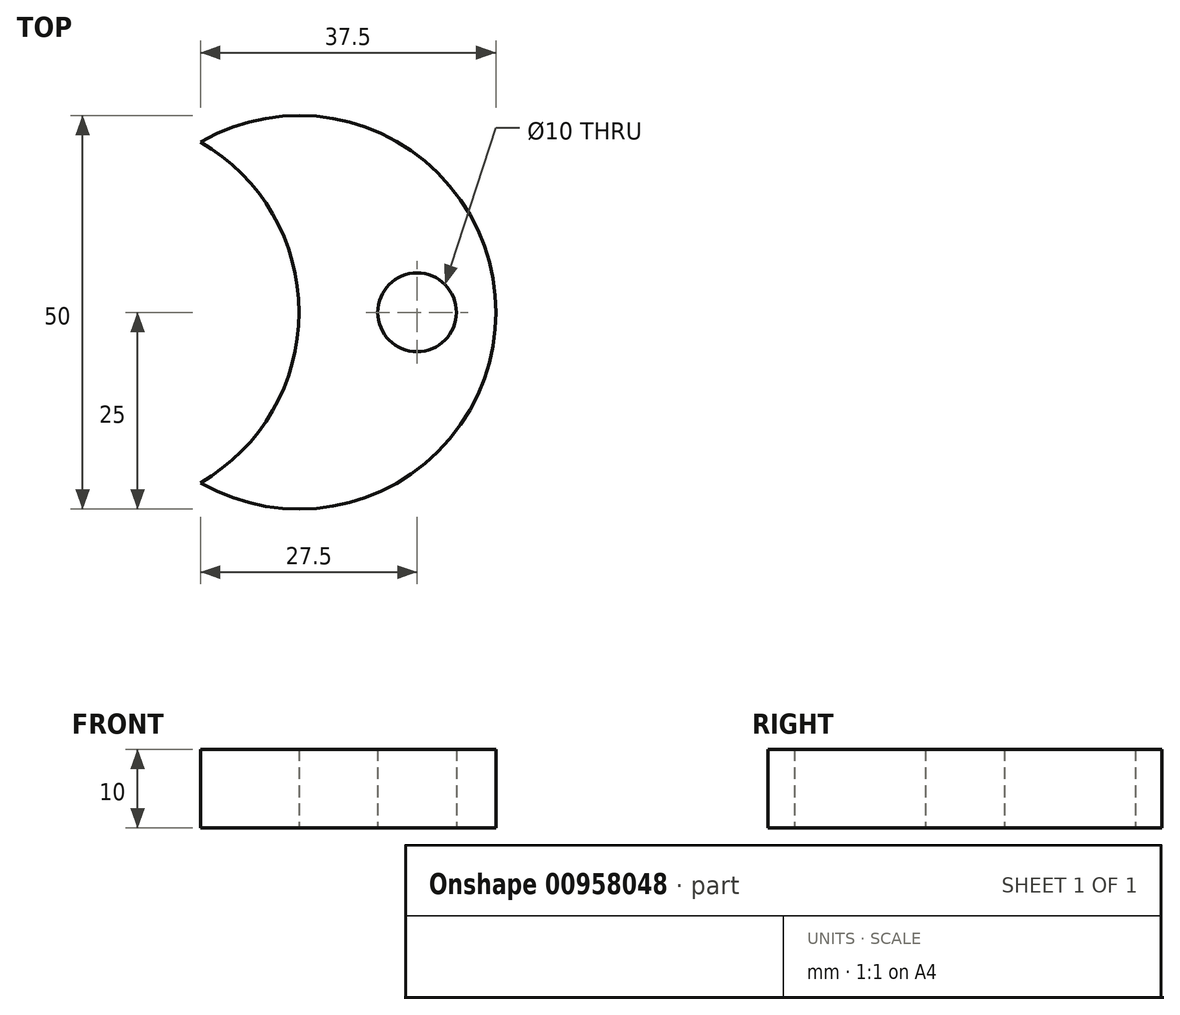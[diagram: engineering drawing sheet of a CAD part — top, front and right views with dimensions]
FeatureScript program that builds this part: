
annotation { "Feature Type Name" : "Feature", "Feature Type Description" : "" }
export const myFeature = defineFeature(function(context is Context, id is Id, definition is map)
    precondition{}
    {
        {
            var Q0;
            Q0=qCreatedBy(makeId("Top.planeOp"),FACE);
            var sketch = newSketch(context, id + "F0", { "sketchPlane" : qUnion([Q0])});
            skCircle(sketch, "E0", {"center": v(0, 0) * mm, "radius": 25 * mm});
            skCircle(sketch, "E1", {"center": v(-25, 0) * mm, "radius": 25 * mm});
            skCircle(sketch, "E2", {"center": v(15, 0) * mm, "radius": 5 * mm});
            skSolve(sketch);
        }
        {
            var Q0;
            {var subQ0=sQuery(id+"F0.wireOp",EDGE,"E1");var subQ1=sQuery(id+"F0.wireOp",EDGE,"E0");var subQ2=makeQuery(id+"F0.imprint","INTERSECT",VERTEX,{"disambiguationData":[OD(0.0)],"derivedFrom":[subQ1,subQ0]});Q0=makeQuery(id+"F0.imprint","IMPRINT",FACE,{"disambiguationData":[TD([[makeQuery(id+"F0.imprint","IMPRINT",EDGE,{"disambiguationData":[TD([[subQ2,-1.0]])],"derivedFrom":subQ1}),1.0]])]});}
            extrude(context, id + "F1", {"entities" : qUnion([Q0]), "depth" : 10 * mm, "offsetDistance" : 25 * mm});
        }
    });
